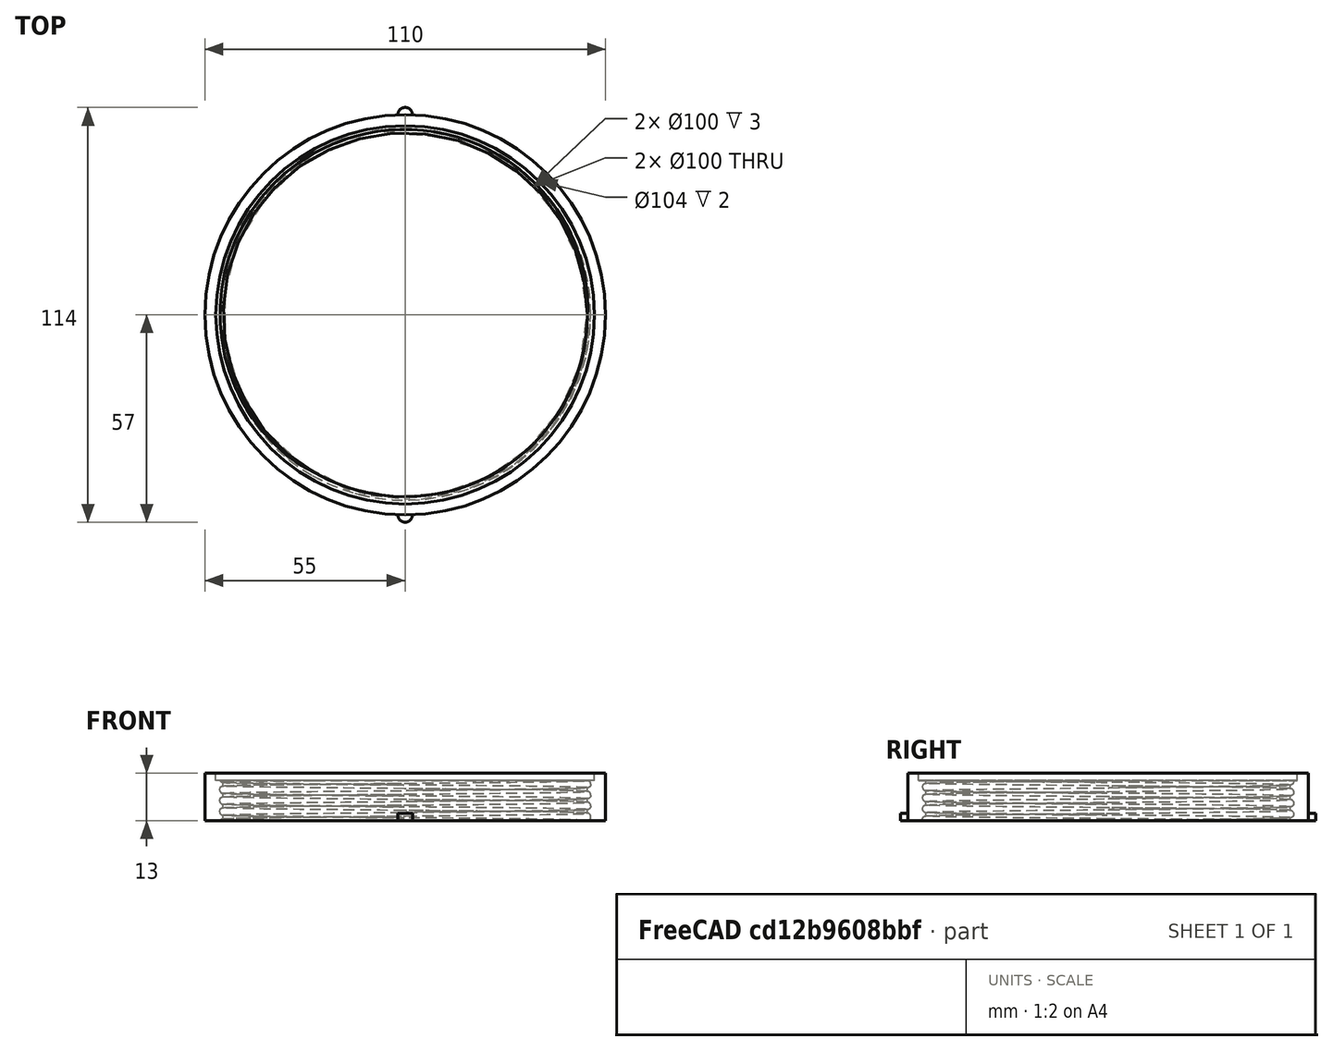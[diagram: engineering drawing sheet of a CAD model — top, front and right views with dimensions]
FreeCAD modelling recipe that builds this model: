
FCSTD DOCUMENT  (FreeCAD 0.17R13522 (Git))
Label: test_tapa_rosca
License: CreativeCommons Attribution-ShareAlike
LicenseURL: http://creativecommons.org/licenses/by-sa/4.0/
objects: Part::Cylinder×5, Part::Cut×3, Part::MultiFuse×3, Part::Feature×1, Part::Box×1
note: 13 computed .brp shape members not serialized (recipe doc carries the construction recipe); baked Part::Feature solids carry a one-line shape summary decoded from their .brp

FEATURE [Part::Feature] Cut017001  label="parte_media001"
  shape: bbox 111 x 119.3 x 50.77 mm, 138 faces (baked)
FEATURE [Part::Box] Box  label="Cube"
  AttacherType = Attacher::AttachEngine3D
  Height = 50
  Length = 500
  Placement = pos=(-77,-69,-16) rot=(0,0,1;0rad)
  Width = 500
FEATURE [Part::Cut] Cut
  Base = -> Cut017001
  Tool = -> Box
FEATURE [Part::Cylinder] Cylinder
  Angle = 360
  AttacherType = Attacher::AttachEngine3D
  Height = 20
  Radius = 55
FEATURE [Part::Cylinder] Cylinder001
  Angle = 360
  AttacherType = Attacher::AttachEngine3D
  Height = 20
  Radius = 52
FEATURE [Part::Cut] Cut017002
  Base = -> Cylinder
  Placement = pos=(0,0,27) rot=(0,0,1;0rad)
  Tool = -> Cylinder001
FEATURE [Part::Cylinder] Cylinder002
  Angle = 360
  AttacherType = Attacher::AttachEngine3D
  Height = 9
  Placement = pos=(0,55,27) rot=(0,0,1;0rad)
  Radius = 2
FEATURE [Part::Cylinder] Cylinder003
  Angle = 360
  AttacherType = Attacher::AttachEngine3D
  Height = 9
  Placement = pos=(0,-55,27) rot=(0,0,1;0rad)
  Radius = 2
FEATURE [Part::Cylinder] Cylinder004
  Angle = 360
  AttacherType = Attacher::AttachEngine3D
  Height = 34
  Radius = 60
FEATURE [Part::MultiFuse] Fusion
  Shapes = -> [Cut017002,Cylinder002]
FEATURE [Part::MultiFuse] Fusion001
  Shapes = -> [Cylinder003,Cut]
FEATURE [Part::MultiFuse] Fusion002
  Shapes = -> [Fusion001,Fusion]
FEATURE [Part::Cut] Cut017003
  Base = -> Fusion002
  Tool = -> Cylinder004
